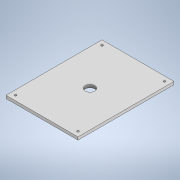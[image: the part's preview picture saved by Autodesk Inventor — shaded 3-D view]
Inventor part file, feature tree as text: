
AUTODESK INVENTOR PART (.ipt)
format: ipt  version: 2020 (Build 240168000, 168)  size: 108,032 bytes
history: native  units: mm
features: extrude x1, sketch x1
ambient origin geometry x8: Origin, YZ Plane, XZ Plane, XY Plane, X Axis, Y Axis, Z Axis, Center Point
bodies: Solide1 (feature_tree)
feature tree (2):
  extrude  "Extrusion1"  Depth=150.0mm
  sketch  "Esquisse1"
